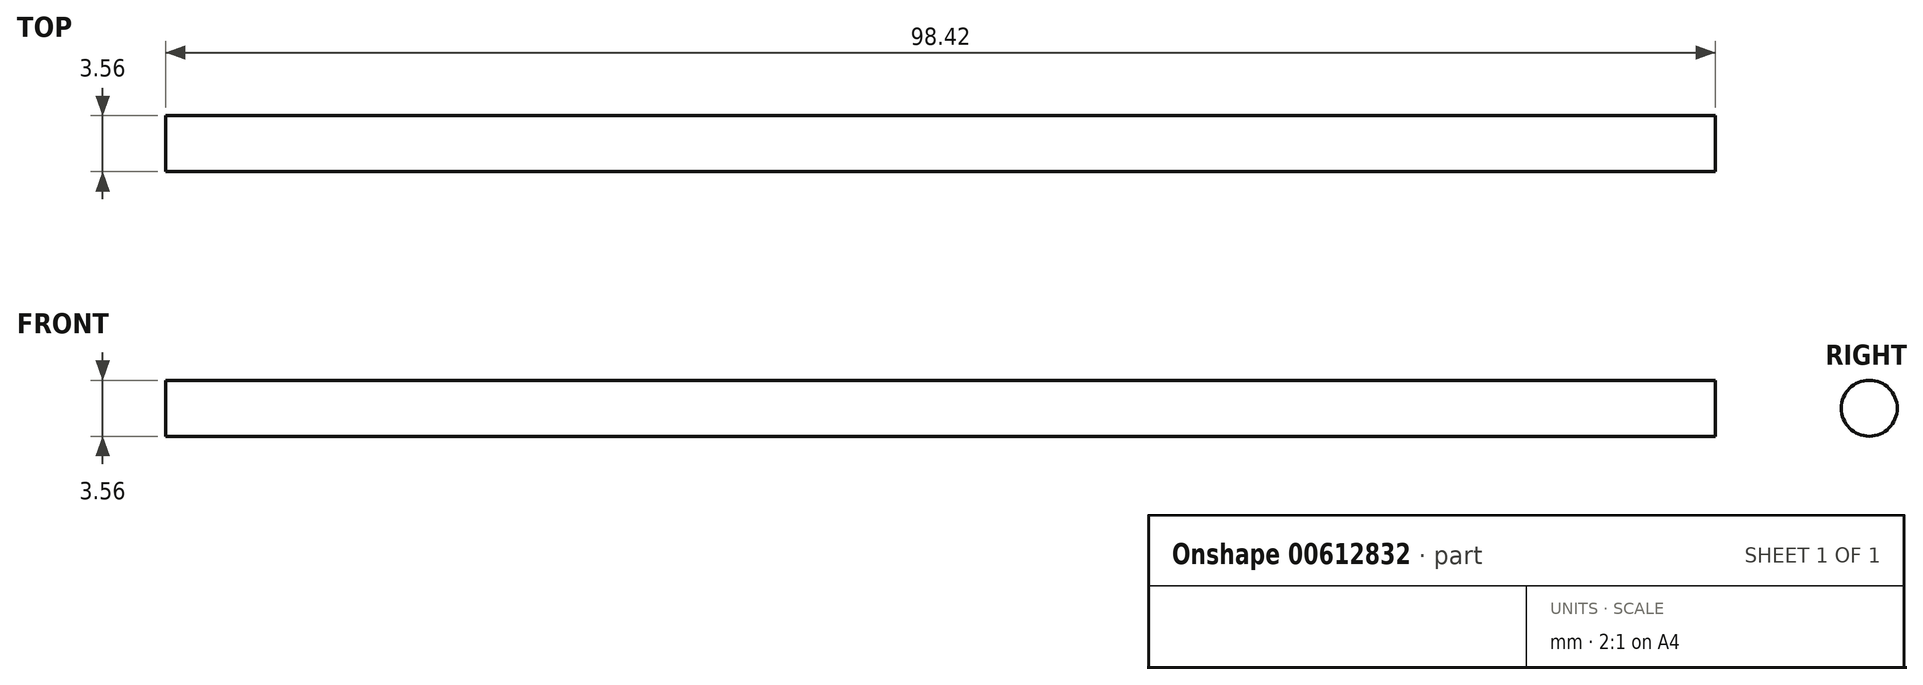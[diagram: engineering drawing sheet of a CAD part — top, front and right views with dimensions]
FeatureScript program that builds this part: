
annotation { "Feature Type Name" : "Feature", "Feature Type Description" : "" }
export const myFeature = defineFeature(function(context is Context, id is Id, definition is map)
    precondition{}
    {
        {
            var Q0;
            Q0=qCreatedBy(makeId("Right.planeOp"),FACE);
            var sketch = newSketch(context, id + "F0", { "sketchPlane" : qUnion([Q0])});
            skCircle(sketch, "E0", {"center": v(0, 0) * mm, "radius": 1.78 * mm});
            skSolve(sketch);
        }
        {
            var Q0;
            Q0=qSketchRegion(id+"F0",true);
            extrude(context, id + "F1", {"entities" : qUnion([Q0]), "depth" : 98.42 * mm, "symmetric" : true});
        }
    });
